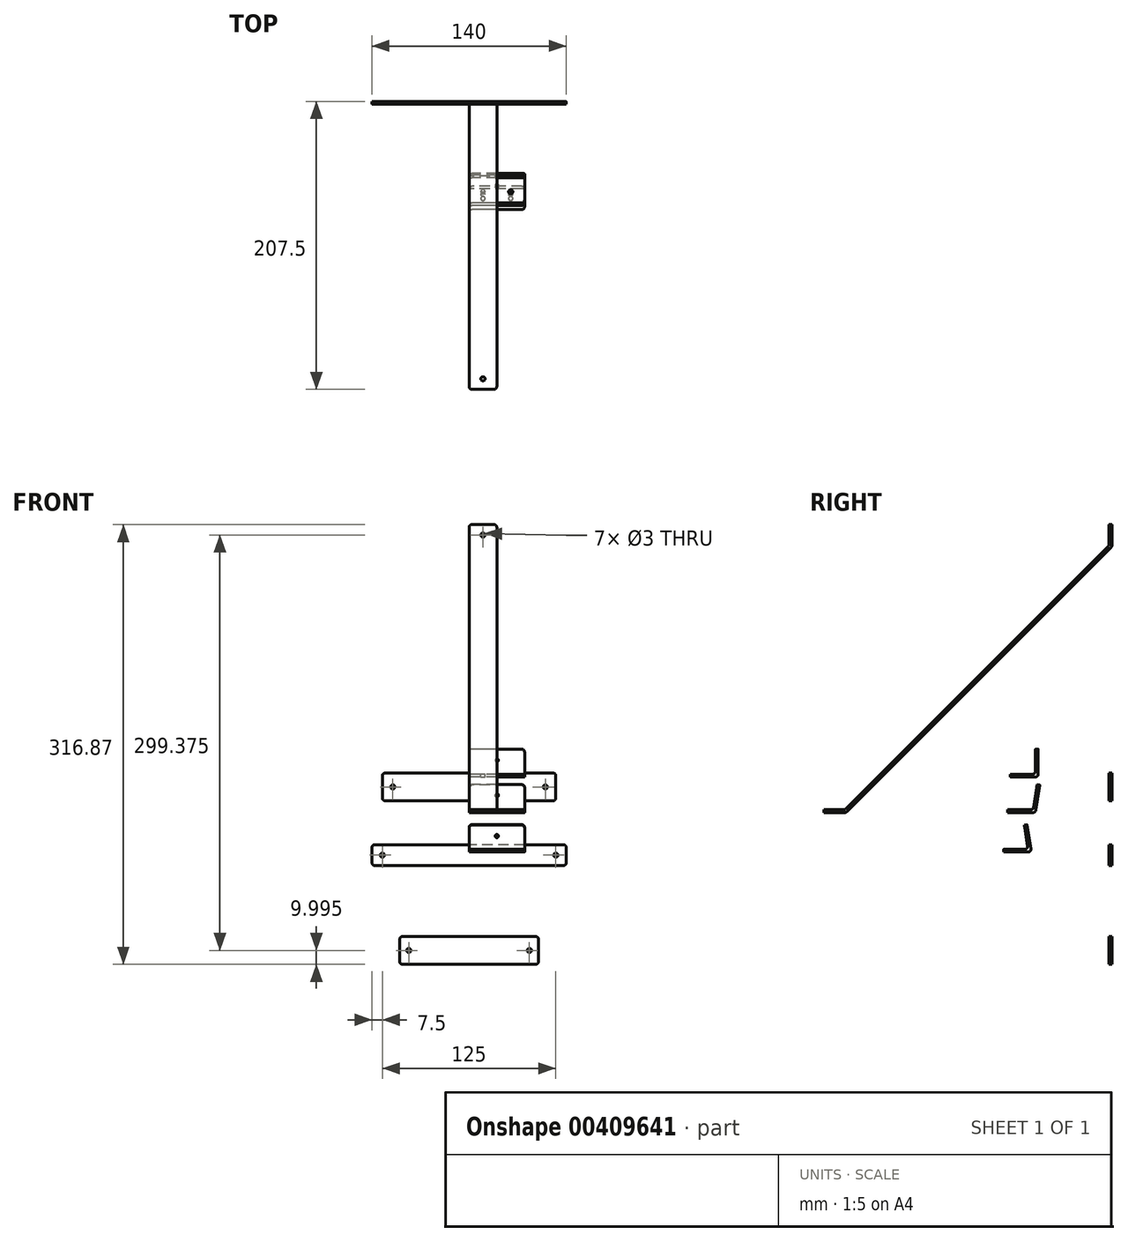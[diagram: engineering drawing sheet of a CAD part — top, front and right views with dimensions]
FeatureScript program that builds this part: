
annotation { "Feature Type Name" : "Feature", "Feature Type Description" : "" }
export const myFeature = defineFeature(function(context is Context, id is Id, definition is map)
    precondition{}
    {
        {
            var Q0;
            Q0=qCreatedBy(makeId("Front.planeOp"),FACE);
            var sketch = newSketch(context, id + "F0", { "sketchPlane" : qUnion([Q0])});
            skLineSegment(sketch, "E0.bottom", {"start": v(62.5, 8.45) * mm, "end": v(-62.5, 8.45) * mm});
            skLineSegment(sketch, "E0.top", {"start": v(62.5, 28.45) * mm, "end": v(-62.5, 28.45) * mm});
            skLineSegment(sketch, "E0.left", {"start": v(62.5, 8.45) * mm, "end": v(62.5, 28.45) * mm});
            skLineSegment(sketch, "E0.right", {"start": v(-62.5, 8.45) * mm, "end": v(-62.5, 28.45) * mm});
            skPoint(sketch, "E0.middle", {"position": v(0, 18.45) * mm});
            skCircle(sketch, "E1", {"center": v(-55, 18.45) * mm, "radius": 1.5 * mm});
            skCircle(sketch, "E2", {"center": v(55, 18.45) * mm, "radius": 1.5 * mm});
            skSolve(sketch);
        }
        {
            var Q0;
            Q0 = qSketchRegion(id + "F0", true);
            extrude(context, id + "F1", {"entities" : qUnion([Q0]), "depth" : 2 * mm});
        }
        {
            var Q0;
            Q0=makeQuery(id+"F1.opExtrude","SWEPT_EDGE",EDGE,{"disambiguationData":[OSD([sQuery(id+"F0.wireOp",EDGE,"E0.top"),sQuery(id+"F0.wireOp",EDGE,"E0.right")])]});
            var Q1;
            Q1=makeQuery(id+"F1.opExtrude","SWEPT_EDGE",EDGE,{"disambiguationData":[OSD([sQuery(id+"F0.wireOp",EDGE,"E0.bottom"),sQuery(id+"F0.wireOp",EDGE,"E0.right")])]});
            var Q2;
            Q2=makeQuery(id+"F1.opExtrude","SWEPT_EDGE",EDGE,{"disambiguationData":[OSD([sQuery(id+"F0.wireOp",EDGE,"E0.top"),sQuery(id+"F0.wireOp",EDGE,"E0.left")])]});
            var Q3;
            Q3=makeQuery(id+"F1.opExtrude","SWEPT_EDGE",EDGE,{"disambiguationData":[OSD([sQuery(id+"F0.wireOp",EDGE,"E0.bottom"),sQuery(id+"F0.wireOp",EDGE,"E0.left")])]});
            fillet(context, id + "F2", {"entities" : qUnion([Q0, Q1, Q2, Q3]), "radius" : 2 * mm, "tangentPropagation" : true, "allowEdgeOverflow" : false});
        }
        {
            var Q0;
            Q0=qCreatedBy(makeId("Front.planeOp"),FACE);
            var sketch = newSketch(context, id + "F3", { "sketchPlane" : qUnion([Q0])});
            skLineSegment(sketch, "E3.bottom", {"start": v(70, -38.18) * mm, "end": v(-70, -38.18) * mm});
            skLineSegment(sketch, "E3.top", {"start": v(70, -23.18) * mm, "end": v(-70, -23.18) * mm});
            skLineSegment(sketch, "E3.left", {"start": v(70, -38.18) * mm, "end": v(70, -23.18) * mm});
            skLineSegment(sketch, "E3.right", {"start": v(-70, -38.18) * mm, "end": v(-70, -23.18) * mm});
            skPoint(sketch, "E3.middle", {"position": v(0, -30.68) * mm});
            skCircle(sketch, "E4", {"center": v(-62.5, -30.68) * mm, "radius": 1.5 * mm});
            skCircle(sketch, "E5", {"center": v(62.5, -30.68) * mm, "radius": 1.5 * mm});
            skCircle(sketch, "E6", {"center": v(-43.45, -30.68) * mm, "radius": 1.5 * mm, "construction": true});
            skCircle(sketch, "E7", {"center": v(43.45, -30.68) * mm, "radius": 1.5 * mm, "construction": true});
            skSolve(sketch);
        }
        {
            var Q0;
            Q0 = qSketchRegion(id + "F3", true);
            extrude(context, id + "F4", {"entities" : qUnion([Q0]), "depth" : 2 * mm});
        }
        {
            var Q0;
            Q0=makeQuery(id+"F4.opExtrude","SWEPT_EDGE",EDGE,{"disambiguationData":[OSD([sQuery(id+"F3.wireOp",EDGE,"E3.top"),sQuery(id+"F3.wireOp",EDGE,"E3.right")])]});
            var Q1;
            Q1=makeQuery(id+"F4.opExtrude","SWEPT_EDGE",EDGE,{"disambiguationData":[OSD([sQuery(id+"F3.wireOp",EDGE,"E3.bottom"),sQuery(id+"F3.wireOp",EDGE,"E3.right")])]});
            var Q2;
            Q2=makeQuery(id+"F4.opExtrude","SWEPT_EDGE",EDGE,{"disambiguationData":[OSD([sQuery(id+"F3.wireOp",EDGE,"E3.top"),sQuery(id+"F3.wireOp",EDGE,"E3.left")])]});
            var Q3;
            Q3=makeQuery(id+"F4.opExtrude","SWEPT_EDGE",EDGE,{"disambiguationData":[OSD([sQuery(id+"F3.wireOp",EDGE,"E3.bottom"),sQuery(id+"F3.wireOp",EDGE,"E3.left")])]});
            fillet(context, id + "F5", {"entities" : qUnion([Q0, Q1, Q2, Q3]), "radius" : 2 * mm, "tangentPropagation" : true, "allowEdgeOverflow" : false});
        }
        {
            var Q0;
            Q0=qCreatedBy(makeId("Right.planeOp"),FACE);
            var sketch = newSketch(context, id + "F6", { "sketchPlane" : qUnion([Q0])});
            skLineSegment(sketch, "E8.bottom", {"start": v(0, 207.5) * mm, "end": v(-2, 207.5) * mm});
            skLineSegment(sketch, "E8.left", {"start": v(0, 207.5) * mm, "end": v(0, 191.67) * mm});
            skLineSegment(sketch, "E8.right", {"start": v(-2, 207.5) * mm, "end": v(-2, 192.5) * mm});
            skLineSegment(sketch, "E9.bottom", {"start": v(-192.5, 2) * mm, "end": v(-207.5, 2) * mm});
            skLineSegment(sketch, "E9.top", {"start": v(-191.67, 0) * mm, "end": v(-207.5, 0) * mm});
            skLineSegment(sketch, "E9.right", {"start": v(-207.5, 2) * mm, "end": v(-207.5, 0) * mm});
            skLineSegment(sketch, "E10", {"start": v(-2, 192.5) * mm, "end": v(-192.5, 2) * mm});
            skLineSegment(sketch, "E11", {"start": v(0, 200) * mm, "end": v(0, 0) * mm, "construction": true});
            skLineSegment(sketch, "E12", {"start": v(0, 0) * mm, "end": v(-200, 0) * mm, "construction": true});
            skLineSegment(sketch, "E13", {"start": v(0, 191.67) * mm, "end": v(-191.67, 0) * mm});
            skSolve(sketch);
        }
        {
            var Q0;
            Q0 = qSketchRegion(id + "F6", true);
            extrude(context, id + "F7", {"entities" : qUnion([Q0]), "depth" : 20 * mm});
        }
        {
            var Q0;
            Q0=makeQuery(id+"F7.opExtrude","SWEPT_FACE",FACE,{"disambiguationData":[OSD([sQuery(id+"F6.wireOp",EDGE,"E8.right")])]});
            var sketch = newSketch(context, id + "F8", { "sketchPlane" : qUnion([Q0])});
            skCircle(sketch, "E14", {"center": v(10, 200) * mm, "radius": 1.5 * mm});
            skSolve(sketch);
        }
        {
            var Q0;
            Q0=makeQuery(id+"F7.opExtrude","SWEPT_FACE",FACE,{"disambiguationData":[OSD([sQuery(id+"F6.wireOp",EDGE,"E9.bottom")])]});
            var sketch = newSketch(context, id + "F9", { "sketchPlane" : qUnion([Q0])});
            skCircle(sketch, "E15", {"center": v(10, -200) * mm, "radius": 1.5 * mm});
            skPoint(sketch, "E15.centerSnap0", {"position": v(10, -192.5) * mm});
            skSolve(sketch);
        }
        {
            var Q0;
            Q0=sQuery(id+"F8.wireOp",VERTEX,"E14.center");
            var Q1;
            Q1=sQuery(id+"F9.wireOp",VERTEX,"E15.center");
            var Q2;
            Q2=makeQuery(id+"F7.opExtrude","SWEPT_BODY",BODY,{"disambiguationData":[OSD([sQuery(id+"F6.wireOp",EDGE,"E8.bottom"),sQuery(id+"F6.wireOp",EDGE,"E8.left"),sQuery(id+"F6.wireOp",EDGE,"E8.right"),sQuery(id+"F6.wireOp",EDGE,"E9.bottom"),sQuery(id+"F6.wireOp",EDGE,"E9.top"),sQuery(id+"F6.wireOp",EDGE,"E9.right"),sQuery(id+"F6.wireOp",EDGE,"E10"),sQuery(id+"F6.wireOp",EDGE,"E13")])]});
            hole(context, id + "F10", {"style" : HoleStyle.SIMPLE, "endStyle" : HoleEndStyle.BLIND, "holeDiameter" : 3 * mm, "holeDepth" : 10 * mm, "tappedDepth" : 12 * mm, "tapClearance" : 3, "locations" : qUnion([Q0, Q1]), "scope" : qUnion([Q2])});
        }
        {
            var Q0;
            Q0=makeQuery(id+"F7.opExtrude","SWEPT_EDGE",EDGE,{"disambiguationData":[OSD([sQuery(id+"F6.wireOp",EDGE,"E8.right"),sQuery(id+"F6.wireOp",EDGE,"E10")])]});
            var Q1;
            Q1=makeQuery(id+"F7.opExtrude","SWEPT_EDGE",EDGE,{"disambiguationData":[OSD([sQuery(id+"F6.wireOp",EDGE,"E8.left"),sQuery(id+"F6.wireOp",EDGE,"E13")])]});
            var Q2;
            Q2=makeQuery(id+"F7.opExtrude","SWEPT_EDGE",EDGE,{"disambiguationData":[OSD([sQuery(id+"F6.wireOp",EDGE,"E9.top"),sQuery(id+"F6.wireOp",EDGE,"E13")])]});
            var Q3;
            Q3=makeQuery(id+"F7.opExtrude","SWEPT_EDGE",EDGE,{"disambiguationData":[OSD([sQuery(id+"F6.wireOp",EDGE,"E9.bottom"),sQuery(id+"F6.wireOp",EDGE,"E10")])]});
            var Q4;
            Q4=makeQuery(id+"F7.opExtrude","CAP_EDGE",EDGE,{"disambiguationData":[OSD([sQuery(id+"F6.wireOp",EDGE,"E8.bottom")])],"isStart":true});
            var Q5;
            Q5=makeQuery(id+"F7.opExtrude","CAP_EDGE",EDGE,{"disambiguationData":[OSD([sQuery(id+"F6.wireOp",EDGE,"E8.bottom")])],"isStart":false});
            var Q6;
            Q6=makeQuery(id+"F7.opExtrude","CAP_EDGE",EDGE,{"disambiguationData":[OSD([sQuery(id+"F6.wireOp",EDGE,"E9.right")])],"isStart":false});
            var Q7;
            Q7=makeQuery(id+"F7.opExtrude","CAP_EDGE",EDGE,{"disambiguationData":[OSD([sQuery(id+"F6.wireOp",EDGE,"E9.right")])],"isStart":true});
            fillet(context, id + "F11", {"entities" : qUnion([Q0, Q1, Q2, Q3, Q4, Q5, Q6, Q7]), "radius" : 2 * mm, "tangentPropagation" : true, "allowEdgeOverflow" : false});
        }
        {
            var Q0;
            Q0=qCreatedBy(makeId("Front.planeOp"),FACE);
            var sketch = newSketch(context, id + "F12", { "sketchPlane" : qUnion([Q0])});
            skLineSegment(sketch, "E16.bottom", {"start": v(50, -109.37) * mm, "end": v(-50, -109.37) * mm});
            skLineSegment(sketch, "E16.top", {"start": v(50, -89.37) * mm, "end": v(-50, -89.37) * mm});
            skLineSegment(sketch, "E16.left", {"start": v(50, -109.37) * mm, "end": v(50, -89.37) * mm});
            skLineSegment(sketch, "E16.right", {"start": v(-50, -109.37) * mm, "end": v(-50, -89.37) * mm});
            skPoint(sketch, "E16.middle", {"position": v(0, -99.37) * mm});
            skCircle(sketch, "E17", {"center": v(-43.45, -99.37) * mm, "radius": 1.5 * mm});
            skCircle(sketch, "E18", {"center": v(43.45, -99.37) * mm, "radius": 1.5 * mm});
            skSolve(sketch);
        }
        {
            var Q0;
            Q0 = qSketchRegion(id + "F12", true);
            extrude(context, id + "F13", {"entities" : qUnion([Q0]), "depth" : 2 * mm});
        }
        {
            var Q0;
            Q0=makeQuery(id+"F13.opExtrude","SWEPT_EDGE",EDGE,{"disambiguationData":[OSD([sQuery(id+"F12.wireOp",EDGE,"E16.top"),sQuery(id+"F12.wireOp",EDGE,"E16.right")])]});
            var Q1;
            Q1=makeQuery(id+"F13.opExtrude","SWEPT_EDGE",EDGE,{"disambiguationData":[OSD([sQuery(id+"F12.wireOp",EDGE,"E16.bottom"),sQuery(id+"F12.wireOp",EDGE,"E16.right")])]});
            var Q2;
            Q2=makeQuery(id+"F13.opExtrude","SWEPT_EDGE",EDGE,{"disambiguationData":[OSD([sQuery(id+"F12.wireOp",EDGE,"E16.top"),sQuery(id+"F12.wireOp",EDGE,"E16.left")])]});
            var Q3;
            Q3=makeQuery(id+"F13.opExtrude","SWEPT_EDGE",EDGE,{"disambiguationData":[OSD([sQuery(id+"F12.wireOp",EDGE,"E16.bottom"),sQuery(id+"F12.wireOp",EDGE,"E16.left")])]});
            fillet(context, id + "F14", {"entities" : qUnion([Q0, Q1, Q2, Q3]), "radius" : 2 * mm, "tangentPropagation" : true, "allowEdgeOverflow" : false});
        }
        {
            var Q0;
            Q0=qCreatedBy(makeId("Right.planeOp"),FACE);
            var sketch = newSketch(context, id + "F15", { "sketchPlane" : qUnion([Q0])});
            skLineSegment(sketch, "E19.bottom", {"start": v(-53.14, 45.65) * mm, "end": v(-55.14, 45.65) * mm});
            skLineSegment(sketch, "E19.top", {"start": v(-53.14, 27.65) * mm, "end": v(-55.14, 27.65) * mm});
            skLineSegment(sketch, "E19.left", {"start": v(-53.14, 45.65) * mm, "end": v(-53.14, 27.65) * mm});
            skLineSegment(sketch, "E19.right", {"start": v(-55.14, 45.65) * mm, "end": v(-55.14, 27.65) * mm});
            skLineSegment(sketch, "E20.bottom", {"start": v(-53.14, 27.65) * mm, "end": v(-73.14, 27.65) * mm});
            skLineSegment(sketch, "E20.top", {"start": v(-53.14, 25.65) * mm, "end": v(-73.14, 25.65) * mm});
            skLineSegment(sketch, "E20.left", {"start": v(-53.14, 27.65) * mm, "end": v(-53.14, 25.65) * mm});
            skLineSegment(sketch, "E20.right", {"start": v(-73.14, 27.65) * mm, "end": v(-73.14, 25.65) * mm});
            skSolve(sketch);
        }
        {
            var Q0;
            Q0 = qSketchRegion(id + "F15", true);
            extrude(context, id + "F16", {"entities" : qUnion([Q0]), "depth" : 40 * mm});
        }
        {
            var Q0;
            Q0=makeQuery(id+"F16.opExtrude","SWEPT_FACE",FACE,{"disambiguationData":[OSD([sQuery(id+"F15.wireOp",EDGE,"E19.right")])]});
            var sketch = newSketch(context, id + "F17", { "sketchPlane" : qUnion([Q0])});
            skCircle(sketch, "E21", {"center": v(20, 37.65) * mm, "radius": 1.2 * mm});
            skSolve(sketch);
        }
        {
            var Q0;
            Q0=makeQuery(id+"F16.opExtrude","SWEPT_FACE",FACE,{"disambiguationData":[OSD([sQuery(id+"F15.wireOp",EDGE,"E20.bottom")])]});
            var sketch = newSketch(context, id + "F18", { "sketchPlane" : qUnion([Q0])});
            skCircle(sketch, "E22", {"center": v(10, -65.14) * mm, "radius": 1.5 * mm});
            skCircle(sketch, "E23", {"center": v(30, -65.14) * mm, "radius": 1.5 * mm});
            skSolve(sketch);
        }
        {
            var Q0;
            Q0=makeQuery(id+"F16.opExtrude","SWEPT_EDGE",EDGE,{"disambiguationData":[OSD([sQuery(id+"F15.wireOp",EDGE,"E19.right"),sQuery(id+"F15.wireOp",EDGE,"E20.bottom")])]});
            var Q1;
            Q1=makeQuery(id+"F16.opExtrude","SWEPT_EDGE",EDGE,{"disambiguationData":[OSD([sQuery(id+"F15.wireOp",EDGE,"E20.top"),sQuery(id+"F15.wireOp",EDGE,"E20.left")])]});
            var Q2;
            Q2=makeQuery(id+"F16.opExtrude","CAP_EDGE",EDGE,{"disambiguationData":[OSD([sQuery(id+"F15.wireOp",EDGE,"E19.bottom")])],"isStart":true});
            var Q3;
            Q3=makeQuery(id+"F16.opExtrude","CAP_EDGE",EDGE,{"disambiguationData":[OSD([sQuery(id+"F15.wireOp",EDGE,"E19.bottom")])],"isStart":false});
            var Q4;
            Q4=makeQuery(id+"F16.opExtrude","CAP_EDGE",EDGE,{"disambiguationData":[OSD([sQuery(id+"F15.wireOp",EDGE,"E20.right")])],"isStart":false});
            var Q5;
            Q5=makeQuery(id+"F16.opExtrude","CAP_EDGE",EDGE,{"disambiguationData":[OSD([sQuery(id+"F15.wireOp",EDGE,"E20.right")])],"isStart":true});
            fillet(context, id + "F19", {"entities" : qUnion([Q0, Q1, Q2, Q3, Q4, Q5]), "radius" : 2 * mm, "tangentPropagation" : true, "allowEdgeOverflow" : false});
        }
        {
            var Q0;
            Q0=qCreatedBy(makeId("Right.planeOp"),FACE);
            var sketch = newSketch(context, id + "F20", { "sketchPlane" : qUnion([Q0])});
            skLineSegment(sketch, "E24.top", {"start": v(-75.09, 0) * mm, "end": v(-55.09, 0) * mm});
            skLineSegment(sketch, "E24.left", {"start": v(-75.09, 2) * mm, "end": v(-75.09, 0) * mm});
            skLineSegment(sketch, "E25", {"start": v(-75.09, 2) * mm, "end": v(-56.8, 2) * mm});
            skLineSegment(sketch, "E26", {"start": v(-56.8, 2) * mm, "end": v(-53.93, 20.07) * mm});
            skLineSegment(sketch, "E27", {"start": v(-53.93, 20.07) * mm, "end": v(-51.96, 19.75) * mm});
            skLineSegment(sketch, "E28", {"start": v(-51.96, 19.75) * mm, "end": v(-55.09, 0) * mm});
            skPoint(sketch, "E29", {"position": v(-53.16, 12.15) * mm});
            skLineSegment(sketch, "E30", {"start": v(-55.09, 0) * mm, "end": v(-55.5, -2.64) * mm, "construction": true});
            skLineSegment(sketch, "E31", {"start": v(-55.5, -2.64) * mm, "end": v(-53.53, -2.95) * mm, "construction": true});
            skLineSegment(sketch, "E32", {"start": v(-53.53, -2.95) * mm, "end": v(-50.78, 14.39) * mm, "construction": true});
            skPoint(sketch, "E33", {"position": v(-51.18, 11.86) * mm});
            skLineSegment(sketch, "E34", {"start": v(-52.3, -3) * mm, "end": v(-61.2, -3) * mm, "construction": true});
            skSolve(sketch);
        }
        {
            var Q0;
            Q0 = qSketchRegion(id + "F20", true);
            extrude(context, id + "F21", {"entities" : qUnion([Q0]), "depth" : 40 * mm});
        }
        {
            var Q0;
            Q0=makeQuery(id+"F21.opExtrude","SWEPT_FACE",FACE,{"disambiguationData":[OSD([sQuery(id+"F20.wireOp",EDGE,"E28")])]});
            var sketch = newSketch(context, id + "F22", { "sketchPlane" : qUnion([Q0])});
            skCircle(sketch, "E35", {"center": v(-20, 3.68) * mm, "radius": 1.2 * mm});
            skSolve(sketch);
        }
        {
            var Q0;
            Q0=makeQuery(id+"F21.opExtrude","SWEPT_FACE",FACE,{"disambiguationData":[OSD([sQuery(id+"F20.wireOp",EDGE,"E25")])]});
            var sketch = newSketch(context, id + "F23", { "sketchPlane" : qUnion([Q0])});
            skCircle(sketch, "E36", {"center": v(10, -67.09) * mm, "radius": 1.5 * mm});
            skCircle(sketch, "E37", {"center": v(30, -67.09) * mm, "radius": 1.5 * mm});
            skSolve(sketch);
        }
        {
            var Q0;
            Q0=makeQuery(id+"F21.opExtrude","SWEPT_EDGE",EDGE,{"disambiguationData":[OSD([sQuery(id+"F20.wireOp",EDGE,"E25"),sQuery(id+"F20.wireOp",EDGE,"E26")])]});
            var Q1;
            Q1=makeQuery(id+"F21.opExtrude","SWEPT_EDGE",EDGE,{"disambiguationData":[OSD([sQuery(id+"F20.wireOp",EDGE,"E24.top"),sQuery(id+"F20.wireOp",EDGE,"E28")])]});
            var Q2;
            Q2=makeQuery(id+"F21.opExtrude","CAP_EDGE",EDGE,{"disambiguationData":[OSD([sQuery(id+"F20.wireOp",EDGE,"E27")])],"isStart":true});
            var Q3;
            Q3=makeQuery(id+"F21.opExtrude","CAP_EDGE",EDGE,{"disambiguationData":[OSD([sQuery(id+"F20.wireOp",EDGE,"E24.left")])],"isStart":true});
            var Q4;
            Q4=makeQuery(id+"F21.opExtrude","CAP_EDGE",EDGE,{"disambiguationData":[OSD([sQuery(id+"F20.wireOp",EDGE,"E24.left")])],"isStart":false});
            var Q5;
            Q5=makeQuery(id+"F21.opExtrude","CAP_EDGE",EDGE,{"disambiguationData":[OSD([sQuery(id+"F20.wireOp",EDGE,"E27")])],"isStart":false});
            fillet(context, id + "F24", {"entities" : qUnion([Q0, Q1, Q2, Q3, Q4, Q5]), "radius" : 2 * mm, "tangentPropagation" : true, "allowEdgeOverflow" : false});
        }
        {
            var Q0;
            Q0=qCreatedBy(makeId("Right.planeOp"),FACE);
            var sketch = newSketch(context, id + "F25", { "sketchPlane" : qUnion([Q0])});
            skLineSegment(sketch, "E38.top", {"start": v(-78.05, -28.5) * mm, "end": v(-58.05, -28.5) * mm});
            skLineSegment(sketch, "E38.left", {"start": v(-78.05, -26.5) * mm, "end": v(-78.05, -28.5) * mm});
            skLineSegment(sketch, "E39", {"start": v(-78.05, -26.5) * mm, "end": v(-60.4, -26.5) * mm});
            skLineSegment(sketch, "E40", {"start": v(-60.4, -26.5) * mm, "end": v(-63.16, -9.06) * mm});
            skLineSegment(sketch, "E41", {"start": v(-63.16, -9.06) * mm, "end": v(-61.18, -8.74) * mm});
            skLineSegment(sketch, "E42", {"start": v(-61.18, -8.74) * mm, "end": v(-58.05, -28.5) * mm});
            skLineSegment(sketch, "E43", {"start": v(-58.05, -28.5) * mm, "end": v(-57.58, -31.46) * mm, "construction": true});
            skLineSegment(sketch, "E44", {"start": v(-57.58, -31.46) * mm, "end": v(-55.6, -31.15) * mm, "construction": true});
            skLineSegment(sketch, "E45", {"start": v(-55.6, -31.15) * mm, "end": v(-58.2, -14.75) * mm, "construction": true});
            skLineSegment(sketch, "E46", {"start": v(-50.6, -31.5) * mm, "end": v(-63.36, -31.5) * mm, "construction": true});
            skPoint(sketch, "E47", {"position": v(-59.93, -16.64) * mm});
            skPoint(sketch, "E48", {"position": v(-57.95, -16.33) * mm});
            skSolve(sketch);
        }
        {
            var Q0;
            Q0 = qSketchRegion(id + "F25", true);
            extrude(context, id + "F26", {"entities" : qUnion([Q0]), "depth" : 40 * mm});
        }
        {
            var Q0;
            Q0=makeQuery(id+"F26.opExtrude","SWEPT_FACE",FACE,{"disambiguationData":[OSD([sQuery(id+"F25.wireOp",EDGE,"E39")])]});
            var sketch = newSketch(context, id + "F27", { "sketchPlane" : qUnion([Q0])});
            skCircle(sketch, "E49", {"center": v(10, -70.05) * mm, "radius": 1.5 * mm});
            skCircle(sketch, "E50", {"center": v(30, -70.05) * mm, "radius": 1.5 * mm});
            skSolve(sketch);
        }
        {
            var Q0;
            Q0=makeQuery(id+"F26.opExtrude","SWEPT_FACE",FACE,{"disambiguationData":[OSD([sQuery(id+"F25.wireOp",EDGE,"E40")])]});
            var sketch = newSketch(context, id + "F28", { "sketchPlane" : qUnion([Q0])});
            skCircle(sketch, "E51", {"center": v(20, -7.06) * mm, "radius": 1.2 * mm});
            skSolve(sketch);
        }
        {
            var Q0;
            Q0=sQuery(id+"F18.wireOp",VERTEX,"E22.center");
            var Q1;
            Q1=sQuery(id+"F18.wireOp",VERTEX,"E23.center");
            var Q2;
            Q2=sQuery(id+"F23.wireOp",VERTEX,"E37.center");
            var Q3;
            Q3=sQuery(id+"F23.wireOp",VERTEX,"E36.center");
            var Q4;
            Q4=sQuery(id+"F27.wireOp",VERTEX,"E49.center");
            var Q5;
            Q5=sQuery(id+"F27.wireOp",VERTEX,"E50.center");
            var Q6;
            Q6=makeQuery(id+"F16.opExtrude","SWEPT_BODY",BODY,{"disambiguationData":[OSD([sQuery(id+"F15.wireOp",EDGE,"E19.bottom"),sQuery(id+"F15.wireOp",EDGE,"E19.left"),sQuery(id+"F15.wireOp",EDGE,"E19.right"),sQuery(id+"F15.wireOp",EDGE,"E20.bottom"),sQuery(id+"F15.wireOp",EDGE,"E20.top"),sQuery(id+"F15.wireOp",EDGE,"E20.left"),sQuery(id+"F15.wireOp",EDGE,"E20.right")])]});
            var Q7;
            Q7=makeQuery(id+"F21.opExtrude","SWEPT_BODY",BODY,{"disambiguationData":[OSD([sQuery(id+"F20.wireOp",EDGE,"E24.top"),sQuery(id+"F20.wireOp",EDGE,"E24.left"),sQuery(id+"F20.wireOp",EDGE,"E25"),sQuery(id+"F20.wireOp",EDGE,"E26"),sQuery(id+"F20.wireOp",EDGE,"E27"),sQuery(id+"F20.wireOp",EDGE,"E28")])]});
            var Q8;
            Q8=makeQuery(id+"F26.opExtrude","SWEPT_BODY",BODY,{"disambiguationData":[OSD([sQuery(id+"F25.wireOp",EDGE,"E38.top"),sQuery(id+"F25.wireOp",EDGE,"E38.left"),sQuery(id+"F25.wireOp",EDGE,"E39"),sQuery(id+"F25.wireOp",EDGE,"E40"),sQuery(id+"F25.wireOp",EDGE,"E41"),sQuery(id+"F25.wireOp",EDGE,"E42")])]});
            hole(context, id + "F29", {"style" : HoleStyle.SIMPLE, "endStyle" : HoleEndStyle.BLIND, "holeDiameter" : 3 * mm, "holeDepth" : 10 * mm, "tappedDepth" : 12 * mm, "tapClearance" : 3, "locations" : qUnion([Q0, Q1, Q2, Q3, Q4, Q5]), "scope" : qUnion([Q6, Q7, Q8])});
        }
        {
            var Q0;
            Q0=sQuery(id+"F17.wireOp",VERTEX,"E21.center");
            var Q1;
            Q1=sQuery(id+"F22.wireOp",VERTEX,"E35.center");
            var Q2;
            Q2=sQuery(id+"F28.wireOp",VERTEX,"E51.center");
            var Q3;
            Q3=makeQuery(id+"F16.opExtrude","SWEPT_BODY",BODY,{"disambiguationData":[OSD([sQuery(id+"F15.wireOp",EDGE,"E19.bottom"),sQuery(id+"F15.wireOp",EDGE,"E19.left"),sQuery(id+"F15.wireOp",EDGE,"E19.right"),sQuery(id+"F15.wireOp",EDGE,"E20.bottom"),sQuery(id+"F15.wireOp",EDGE,"E20.top"),sQuery(id+"F15.wireOp",EDGE,"E20.left"),sQuery(id+"F15.wireOp",EDGE,"E20.right")])]});
            var Q4;
            Q4=makeQuery(id+"F21.opExtrude","SWEPT_BODY",BODY,{"disambiguationData":[OSD([sQuery(id+"F20.wireOp",EDGE,"E24.top"),sQuery(id+"F20.wireOp",EDGE,"E24.left"),sQuery(id+"F20.wireOp",EDGE,"E25"),sQuery(id+"F20.wireOp",EDGE,"E26"),sQuery(id+"F20.wireOp",EDGE,"E27"),sQuery(id+"F20.wireOp",EDGE,"E28")])]});
            var Q5;
            Q5=makeQuery(id+"F26.opExtrude","SWEPT_BODY",BODY,{"disambiguationData":[OSD([sQuery(id+"F25.wireOp",EDGE,"E38.top"),sQuery(id+"F25.wireOp",EDGE,"E38.left"),sQuery(id+"F25.wireOp",EDGE,"E39"),sQuery(id+"F25.wireOp",EDGE,"E40"),sQuery(id+"F25.wireOp",EDGE,"E41"),sQuery(id+"F25.wireOp",EDGE,"E42")])]});
            hole(context, id + "F30", {"style" : HoleStyle.SIMPLE, "endStyle" : HoleEndStyle.BLIND, "holeDiameter" : 2.4 * mm, "holeDepth" : 10 * mm, "tappedDepth" : 12 * mm, "tapClearance" : 3, "locations" : qUnion([Q0, Q1, Q2]), "scope" : qUnion([Q3, Q4, Q5])});
        }
        {
            var Q0;
            Q0=makeQuery(id+"F26.opExtrude","SWEPT_EDGE",EDGE,{"disambiguationData":[OSD([sQuery(id+"F25.wireOp",EDGE,"E39"),sQuery(id+"F25.wireOp",EDGE,"E40")])]});
            var Q1;
            Q1=makeQuery(id+"F26.opExtrude","SWEPT_EDGE",EDGE,{"disambiguationData":[OSD([sQuery(id+"F25.wireOp",EDGE,"E38.top"),sQuery(id+"F25.wireOp",EDGE,"E42")])]});
            var Q2;
            Q2=makeQuery(id+"F26.opExtrude","CAP_EDGE",EDGE,{"disambiguationData":[OSD([sQuery(id+"F25.wireOp",EDGE,"E41")])],"isStart":false});
            var Q3;
            Q3=makeQuery(id+"F26.opExtrude","CAP_EDGE",EDGE,{"disambiguationData":[OSD([sQuery(id+"F25.wireOp",EDGE,"E41")])],"isStart":true});
            var Q4;
            Q4=makeQuery(id+"F26.opExtrude","CAP_EDGE",EDGE,{"disambiguationData":[OSD([sQuery(id+"F25.wireOp",EDGE,"E38.left")])],"isStart":true});
            var Q5;
            Q5=makeQuery(id+"F26.opExtrude","CAP_EDGE",EDGE,{"disambiguationData":[OSD([sQuery(id+"F25.wireOp",EDGE,"E38.left")])],"isStart":false});
            fillet(context, id + "F31", {"entities" : qUnion([Q0, Q1, Q2, Q3, Q4, Q5]), "radius" : 2 * mm, "tangentPropagation" : true, "allowEdgeOverflow" : false});
        }
    });
